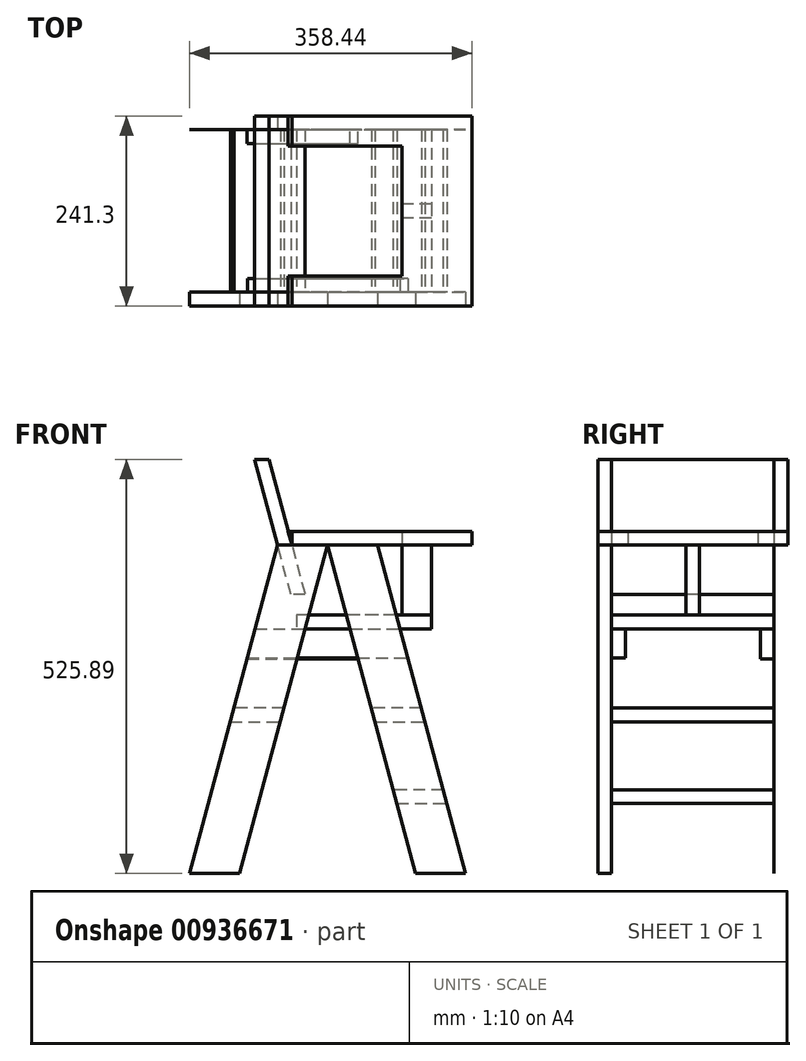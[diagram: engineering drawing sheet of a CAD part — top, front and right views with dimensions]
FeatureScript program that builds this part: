
annotation { "Feature Type Name" : "Feature", "Feature Type Description" : "" }
export const myFeature = defineFeature(function(context is Context, id is Id, definition is map)
    precondition{}
    {
        {
            var Q0;
            Q0=qCreatedBy(makeId("Front.planeOp"),FACE);
            var sketch = newSketch(context, id + "F0", { "sketchPlane" : qUnion([Q0])});
            skLineSegment(sketch, "E0", {"start": v(0, 0) * mm, "end": v(63.5, 0) * mm});
            skLineSegment(sketch, "E1", {"start": v(63.5, 0) * mm, "end": v(175.26, 417.09) * mm});
            skLineSegment(sketch, "E2", {"start": v(175.26, 417.09) * mm, "end": v(111.76, 417.09) * mm});
            skLineSegment(sketch, "E3", {"start": v(111.76, 417.09) * mm, "end": v(0, 0) * mm});
            skLineSegment(sketch, "E4", {"start": v(287.02, 0) * mm, "end": v(350.52, 0) * mm});
            skLineSegment(sketch, "E5", {"start": v(350.52, 0) * mm, "end": v(238.76, 417.09) * mm});
            skLineSegment(sketch, "E6", {"start": v(238.76, 417.09) * mm, "end": v(175.26, 417.09) * mm});
            skLineSegment(sketch, "E7", {"start": v(175.26, 417.09) * mm, "end": v(287.02, 0) * mm});
            skSolve(sketch);
        }
        {
            var Q0;
            Q0 = qSketchRegion(id + "F0", true);
            extrude(context, id + "F1", {"entities" : qUnion([Q0]), "oppositeDirection" : true, "depth" : 17.46 * mm, "offsetDistance" : 25.4 * mm});
        }
        {
            var Q0;
            Q0=makeQuery(id+"F1.opExtrude","CAP_FACE",FACE,{"disambiguationData":[OSD([sQuery(id+"F0.wireOp",EDGE,"E0"),sQuery(id+"F0.wireOp",EDGE,"E1"),sQuery(id+"F0.wireOp",EDGE,"E2"),sQuery(id+"F0.wireOp",EDGE,"E3")])],"isStart":false});
            cPlane(context, id + "F2", {"entities" : qUnion([Q0]), "cplaneType" : CPlaneType.OFFSET, "offset" : 0 * mm, "width" : 152.4 * mm, "height" : 152.4 * mm});
        }
        {
            var Q0;
            Q0=makeQuery(id+"F1.opExtrude","SWEPT_FACE",FACE,{"disambiguationData":[OSD([sQuery(id+"F0.wireOp",EDGE,"E2")])]});
            cPlane(context, id + "F3", {"entities" : qUnion([Q0]), "cplaneType" : CPlaneType.OFFSET, "offset" : 0 * mm, "width" : 152.4 * mm, "height" : 152.4 * mm});
        }
        {
            var Q0;
            Q0=qCreatedBy(id+"F2.planeOp",FACE);
            var sketch = newSketch(context, id + "F4", { "sketchPlane" : qUnion([Q0])});
            skLineSegment(sketch, "E8", {"start": v(-146.7, 354.15) * mm, "end": v(-128.62, 354.15) * mm});
            skLineSegment(sketch, "E9", {"start": v(-128.62, 354.15) * mm, "end": v(-82.6, 525.9) * mm});
            skLineSegment(sketch, "E10", {"start": v(-82.6, 525.9) * mm, "end": v(-100.68, 525.9) * mm});
            skLineSegment(sketch, "E11", {"start": v(-100.68, 525.9) * mm, "end": v(-146.7, 354.15) * mm});
            skPoint(sketch, "E12.0", {"position": v(-111.76, 417.09) * mm});
            skLineSegment(sketch, "E13.0", {"start": v(-129.84, 417.09) * mm, "end": v(-111.76, 417.09) * mm});
            skSolve(sketch);
        }
        {
            var Q0;
            Q0 = qSketchRegion(id + "F4", true);
            extrude(context, id + "F5", {"entities" : qUnion([Q0]), "depth" : 206.38 * mm, "offsetDistance" : 25.4 * mm});
        }
        {
            var Q0;
            Q0=qCreatedBy(id+"F3.planeOp",FACE);
            var sketch = newSketch(context, id + "F6", { "sketchPlane" : qUnion([Q0])});
            skLineSegment(sketch, "E14", {"start": v(129.84, 0) * mm, "end": v(358.44, 0) * mm});
            skLineSegment(sketch, "E15", {"start": v(358.44, 0) * mm, "end": v(358.44, 241.3) * mm});
            skLineSegment(sketch, "E16", {"start": v(358.44, 241.3) * mm, "end": v(129.84, 241.3) * mm});
            skLineSegment(sketch, "E17", {"start": v(129.84, 241.3) * mm, "end": v(129.84, 203.2) * mm});
            skLineSegment(sketch, "E18", {"start": v(129.84, 203.2) * mm, "end": v(269.54, 203.2) * mm});
            skLineSegment(sketch, "E19", {"start": v(269.54, 203.2) * mm, "end": v(269.54, 38.1) * mm});
            skLineSegment(sketch, "E20", {"start": v(269.54, 38.1) * mm, "end": v(129.84, 38.1) * mm});
            skLineSegment(sketch, "E21", {"start": v(129.84, 38.1) * mm, "end": v(129.84, 0) * mm});
            skLineSegment(sketch, "E22.0", {"start": v(175.26, 17.46) * mm, "end": v(111.76, 17.46) * mm});
            skLineSegment(sketch, "E23", {"start": v(143.5, 17.46) * mm, "end": v(129.84, 17.46) * mm});
            skSolve(sketch);
        }
        {
            var Q0;
            Q0 = qSketchRegion(id + "F6", true);
            extrude(context, id + "F7", {"entities" : qUnion([Q0]), "depth" : 17.46 * mm, "offsetDistance" : 25.4 * mm});
        }
        {
            var Q0;
            Q0=makeQuery(id+"F7.opExtrude","SWEPT_FACE",FACE,{"disambiguationData":[OSD([sQuery(id+"F6.wireOp",EDGE,"E21")])]});
            var Q1;
            Q1=makeQuery(id+"F7.opExtrude","SWEPT_FACE",FACE,{"disambiguationData":[OSD([sQuery(id+"F6.wireOp",EDGE,"E17")])]});
            var Q2;
            Q2=makeQuery(id+"F5.opExtrude","SWEPT_FACE",FACE,{"disambiguationData":[OSD([sQuery(id+"F4.wireOp",EDGE,"E11")])]});
            extrude(context, id + "F8", {"entities" : qUnion([Q0, Q1]), "endBound" : BoundingType.UP_TO_SURFACE, "depth" : 25.4 * mm, "endBoundEntityFace" : qUnion([Q2]), "offsetDistance" : 25.4 * mm});
        }
        {
            var Q0;
            Q0=makeQuery(id+"F1.opExtrude","CAP_FACE",FACE,{"disambiguationData":[OSD([sQuery(id+"F0.wireOp",EDGE,"E4"),sQuery(id+"F0.wireOp",EDGE,"E5"),sQuery(id+"F0.wireOp",EDGE,"E6"),sQuery(id+"F0.wireOp",EDGE,"E7")])],"isStart":false});
            var sketch = newSketch(context, id + "F9", { "sketchPlane" : qUnion([Q0])});
            skLineSegment(sketch, "E24.0.1", {"start": v(-135.58, 310.72) * mm, "end": v(-307.03, 310.72) * mm});
            skLineSegment(sketch, "E24.0.2", {"start": v(-307.03, 310.72) * mm, "end": v(-307.03, 328.19) * mm});
            skLineSegment(sketch, "E24.0.3", {"start": v(-307.03, 328.19) * mm, "end": v(-135.58, 328.19) * mm});
            skLineSegment(sketch, "E25.0", {"start": v(-135.58, 328.19) * mm, "end": v(-135.58, 310.72) * mm});
            skLineSegment(sketch, "E26.0", {"start": v(-63.5, 0) * mm, "end": v(-175.26, 417.09) * mm});
            skPoint(sketch, "E27", {"position": v(-146.76, 310.72) * mm});
            skLineSegment(sketch, "E28.0", {"start": v(-100.68, 525.9) * mm, "end": v(-146.7, 354.15) * mm});
            skLineSegment(sketch, "E29", {"start": v(-146.7, 354.15) * mm, "end": v(-153.66, 328.19) * mm});
            skLineSegment(sketch, "E30.0", {"start": v(-128.62, 354.15) * mm, "end": v(-82.6, 525.9) * mm});
            skLineSegment(sketch, "E31", {"start": v(-128.62, 354.15) * mm, "end": v(-135.58, 328.19) * mm});
            skSolve(sketch);
        }
        {
            var Q0;
            {var subQ0=sQuery(id+"F9.wireOp",EDGE,"E25.0");Q0=makeQuery(id+"F9.imprint","IMPRINT",FACE,{"disambiguationData":[TD([[makeQuery(id+"F9.imprint","IMPRINT",EDGE,{"derivedFrom":subQ0}),-1.0]])]});}
            var Q1;
            {var subQ0=sQuery(id+"F9.wireOp",EDGE,"E26.0");var subQ1=sQuery(id+"F9.wireOp",EDGE,"E24.0.1");var subQ2=makeQuery(id+"F9.imprint","INTERSECT",VERTEX,{"derivedFrom":[subQ1,subQ0]});Q1=makeQuery(id+"F9.imprint","IMPRINT",FACE,{"disambiguationData":[TD([[makeQuery(id+"F9.imprint","IMPRINT",EDGE,{"disambiguationData":[TD([[subQ2,-1.0]])],"derivedFrom":subQ1}),-1.0]])]});}
            var Q2;
            {var subQ0=sQuery(id+"F9.wireOp",EDGE,"E24.0.1");var subQ1=makeQuery(id+"F1.opExtrude","CAP_EDGE",EDGE,{"disambiguationData":[OSD([sQuery(id+"F0.wireOp",EDGE,"E7")])],"isStart":false});var subQ2=makeQuery(id+"F9.imprint","INTERSECT",VERTEX,{"derivedFrom":[subQ1,subQ0]});Q2=makeQuery(id+"F9.imprint","IMPRINT",FACE,{"disambiguationData":[TD([[makeQuery(id+"F9.imprint","IMPRINT",EDGE,{"disambiguationData":[TD([[subQ2,-1.0]])],"derivedFrom":subQ0}),-1.0]])]});}
            var Q3;
            {var subQ0=sQuery(id+"F9.wireOp",EDGE,"E24.0.2");Q3=makeQuery(id+"F9.imprint","IMPRINT",FACE,{"disambiguationData":[TD([[makeQuery(id+"F9.imprint","IMPRINT",EDGE,{"derivedFrom":subQ0}),-1.0]])]});}
            extrude(context, id + "F10", {"entities" : qUnion([Q0, Q1, Q2, Q3]), "depth" : 206.38 * mm, "offsetDistance" : 25.4 * mm});
        }
        {
            var Q0;
            Q0=makeQuery(id+"F1.opExtrude","CAP_FACE",FACE,{"disambiguationData":[OSD([sQuery(id+"F0.wireOp",EDGE,"E0"),sQuery(id+"F0.wireOp",EDGE,"E1"),sQuery(id+"F0.wireOp",EDGE,"E2"),sQuery(id+"F0.wireOp",EDGE,"E3")])],"isStart":false});
            var sketch = newSketch(context, id + "F11", { "sketchPlane" : qUnion([Q0])});
            skLineSegment(sketch, "E32.0", {"start": v(-83.26, 310.72) * mm, "end": v(-73.32, 273.64) * mm});
            skLineSegment(sketch, "E33.0", {"start": v(-277.2, 273.64) * mm, "end": v(-267.26, 310.72) * mm});
            skLineSegment(sketch, "E34.0", {"start": v(-135.58, 310.72) * mm, "end": v(-267.26, 310.72) * mm});
            skLineSegment(sketch, "E35", {"start": v(-135.58, 310.72) * mm, "end": v(-83.26, 310.72) * mm});
            skLineSegment(sketch, "E36", {"start": v(-73.32, 273.64) * mm, "end": v(-277.2, 273.64) * mm});
            skSolve(sketch);
        }
        {
            var Q0;
            Q0 = qSketchRegion(id + "F11", true);
            extrude(context, id + "F12", {"entities" : qUnion([Q0]), "depth" : 17.46 * mm, "offsetDistance" : 25.4 * mm});
        }
        {
            var Q0;
            Q0=makeQuery(id+"F10.opExtrude","CAP_FACE",FACE,{"disambiguationData":[OSD([sQuery(id+"F9.wireOp",EDGE,"E24.0.1"),sQuery(id+"F9.wireOp",EDGE,"E24.0.2"),sQuery(id+"F9.wireOp",EDGE,"E24.0.3"),sQuery(id+"F9.wireOp",EDGE,"E25.0")])],"isStart":false});
            var sketch = newSketch(context, id + "F13", { "sketchPlane" : qUnion([Q0])});
            skLineSegment(sketch, "E37.0.0", {"start": v(-175.26, 417.09) * mm, "end": v(-238.76, 417.09) * mm});
            skLineSegment(sketch, "E37.0.1", {"start": v(-238.76, 417.09) * mm, "end": v(-350.52, 0) * mm});
            skLineSegment(sketch, "E37.0.2", {"start": v(-350.52, 0) * mm, "end": v(-287.02, 0) * mm});
            skLineSegment(sketch, "E37.0.3", {"start": v(-287.02, 0) * mm, "end": v(-175.26, 417.09) * mm});
            skLineSegment(sketch, "E38.0.0", {"start": v(-111.76, 417.09) * mm, "end": v(-175.26, 417.09) * mm});
            skLineSegment(sketch, "E38.0.1", {"start": v(-175.26, 417.09) * mm, "end": v(-63.5, 0) * mm});
            skLineSegment(sketch, "E38.0.2", {"start": v(-63.5, 0) * mm, "end": v(0, 0) * mm});
            skLineSegment(sketch, "E38.0.3", {"start": v(0, 0) * mm, "end": v(-111.76, 417.09) * mm});
            skSolve(sketch);
        }
        {
            var Q0;
            Q0 = qSketchRegion(id + "F13", true);
            extrude(context, id + "F14", {"entities" : qUnion([Q0]), "depth" : 11 / 406.4 * mm, "offsetDistance" : 25.4 * mm});
        }
        {
            var Q0;
            {var subQ0=sQuery(id+"F4.wireOp",EDGE,"E10");Q0=makeQuery(id+"F4.imprint","IMPRINT",FACE,{"disambiguationData":[TD([[makeQuery(id+"F4.imprint","IMPRINT",EDGE,{"derivedFrom":subQ0}),1.0]])]});}
            extrude(context, id + "F15", {"entities" : qUnion([Q0]), "oppositeDirection" : true, "depth" : 17.46 * mm, "offsetDistance" : 25.4 * mm});
        }
        {
            var Q0;
            Q0=makeQuery(id+"F5.opExtrude","CAP_FACE",FACE,{"disambiguationData":[OSD([sQuery(id+"F4.wireOp",EDGE,"E8"),sQuery(id+"F4.wireOp",EDGE,"E9"),sQuery(id+"F4.wireOp",EDGE,"E10"),sQuery(id+"F4.wireOp",EDGE,"E11")])],"isStart":false});
            var sketch = newSketch(context, id + "F16", { "sketchPlane" : qUnion([Q0])});
            skLineSegment(sketch, "E39.0.0", {"start": v(-128.62, 354.15) * mm, "end": v(-82.6, 525.9) * mm});
            skLineSegment(sketch, "E39.0.1", {"start": v(-82.6, 525.9) * mm, "end": v(-100.68, 525.9) * mm});
            skLineSegment(sketch, "E39.0.2", {"start": v(-100.68, 525.9) * mm, "end": v(-146.7, 354.15) * mm});
            skLineSegment(sketch, "E39.0.3", {"start": v(-146.7, 354.15) * mm, "end": v(-128.62, 354.15) * mm});
            skLineSegment(sketch, "E40.0", {"start": v(-111.76, 417.09) * mm, "end": v(-175.26, 417.09) * mm});
            skSolve(sketch);
        }
        {
            var Q0;
            {var subQ0=sQuery(id+"F16.wireOp",EDGE,"E39.0.1");Q0=makeQuery(id+"F16.imprint","IMPRINT",FACE,{"disambiguationData":[TD([[makeQuery(id+"F16.imprint","IMPRINT",EDGE,{"derivedFrom":subQ0}),1.0]])]});}
            extrude(context, id + "F17", {"entities" : qUnion([Q0]), "depth" : 17.46 * mm, "offsetDistance" : 25.4 * mm});
        }
        {
            var Q0;
            Q0=makeQuery(id+"F14.opExtrude","CAP_FACE",FACE,{"disambiguationData":[OSD([sQuery(id+"F13.wireOp",EDGE,"E38.0.0"),sQuery(id+"F13.wireOp",EDGE,"E38.0.1"),sQuery(id+"F13.wireOp",EDGE,"E38.0.2"),sQuery(id+"F13.wireOp",EDGE,"E38.0.3")])],"isStart":true});
            var sketch = newSketch(context, id + "F18", { "sketchPlane" : qUnion([Q0])});
            skLineSegment(sketch, "E41.0.0", {"start": v(175.26, 417.09) * mm, "end": v(111.76, 417.09) * mm});
            skLineSegment(sketch, "E41.0.1", {"start": v(111.76, 417.09) * mm, "end": v(0, 0) * mm});
            skLineSegment(sketch, "E41.0.2", {"start": v(0, 0) * mm, "end": v(63.5, 0) * mm});
            skLineSegment(sketch, "E41.0.3", {"start": v(63.5, 0) * mm, "end": v(175.26, 417.09) * mm});
            skLineSegment(sketch, "E42.0.0", {"start": v(287.02, 0) * mm, "end": v(350.52, 0) * mm});
            skLineSegment(sketch, "E42.0.1", {"start": v(350.52, 0) * mm, "end": v(238.76, 417.09) * mm});
            skLineSegment(sketch, "E42.0.2", {"start": v(238.76, 417.09) * mm, "end": v(175.26, 417.09) * mm});
            skLineSegment(sketch, "E42.0.3", {"start": v(175.26, 417.09) * mm, "end": v(287.02, 0) * mm});
            skLineSegment(sketch, "E43.0", {"start": v(135.58, 310.72) * mm, "end": v(307.03, 310.72) * mm});
            skLineSegment(sketch, "E44", {"start": v(135.58, 310.72) * mm, "end": v(83.26, 310.72) * mm});
            skLineSegment(sketch, "E45", {"start": v(83.26, 310.72) * mm, "end": v(73.05, 272.62) * mm});
            skLineSegment(sketch, "E46", {"start": v(73.05, 272.62) * mm, "end": v(277.47, 272.62) * mm});
            skLineSegment(sketch, "E47", {"start": v(277.47, 272.62) * mm, "end": v(267.26, 310.72) * mm});
            skSolve(sketch);
        }
        {
            var Q0;
            {var subQ1=sQuery(id+"F18.wireOp",EDGE,"E44");Q0=makeQuery(id+"F18.imprint","IMPRINT",FACE,{"disambiguationData":[TD([[makeQuery(id+"F18.imprint","IMPRINT",EDGE,{"derivedFrom":subQ1}),1.0]])]});}
            var Q1;
            {var subQ0=sQuery(id+"F18.wireOp",EDGE,"E46");var subQ1=sQuery(id+"F18.wireOp",EDGE,"E41.0.3");var subQ2=makeQuery(id+"F18.imprint","INTERSECT",VERTEX,{"derivedFrom":[subQ1,subQ0]});Q1=makeQuery(id+"F18.imprint","IMPRINT",FACE,{"disambiguationData":[TD([[makeQuery(id+"F18.imprint","IMPRINT",EDGE,{"disambiguationData":[TD([[subQ2,1.0]])],"derivedFrom":subQ1}),1.0]])]});}
            var Q2;
            {var subQ5=sQuery(id+"F18.wireOp",EDGE,"E47");Q2=makeQuery(id+"F18.imprint","IMPRINT",FACE,{"disambiguationData":[TD([[makeQuery(id+"F18.imprint","IMPRINT",EDGE,{"derivedFrom":subQ5}),1.0]])]});}
            extrude(context, id + "F19", {"entities" : qUnion([Q0, Q1, Q2]), "depth" : 17.46 * mm, "offsetDistance" : 25.4 * mm});
        }
        {
            var Q0;
            Q0=makeQuery(id+"F1.opExtrude","CAP_FACE",FACE,{"disambiguationData":[OSD([sQuery(id+"F0.wireOp",EDGE,"E4"),sQuery(id+"F0.wireOp",EDGE,"E5"),sQuery(id+"F0.wireOp",EDGE,"E6"),sQuery(id+"F0.wireOp",EDGE,"E7")])],"isStart":false});
            var sketch = newSketch(context, id + "F20", { "sketchPlane" : qUnion([Q0])});
            skLineSegment(sketch, "E48.0.0", {"start": v(-175.26, 417.09) * mm, "end": v(-238.76, 417.09) * mm});
            skLineSegment(sketch, "E48.0.1", {"start": v(-238.76, 417.09) * mm, "end": v(-350.52, 0) * mm});
            skLineSegment(sketch, "E48.0.2", {"start": v(-350.52, 0) * mm, "end": v(-287.02, 0) * mm});
            skLineSegment(sketch, "E48.0.3", {"start": v(-287.02, 0) * mm, "end": v(-175.26, 417.09) * mm});
            skLineSegment(sketch, "E49", {"start": v(-294.2, 210.14) * mm, "end": v(-230.7, 210.14) * mm});
            skLineSegment(sketch, "E50", {"start": v(-230.7, 210.14) * mm, "end": v(-235.39, 192.68) * mm});
            skLineSegment(sketch, "E51", {"start": v(-235.39, 192.68) * mm, "end": v(-298.89, 192.68) * mm});
            skLineSegment(sketch, "E52", {"start": v(-298.89, 192.68) * mm, "end": v(-294.2, 210.14) * mm});
            skLineSegment(sketch, "E53", {"start": v(-322.02, 106.36) * mm, "end": v(-258.52, 106.36) * mm});
            skLineSegment(sketch, "E54", {"start": v(-258.52, 106.36) * mm, "end": v(-263.2, 88.9) * mm});
            skLineSegment(sketch, "E55", {"start": v(-263.2, 88.9) * mm, "end": v(-326.7, 88.9) * mm});
            skLineSegment(sketch, "E56", {"start": v(-326.7, 88.9) * mm, "end": v(-322.02, 106.36) * mm});
            skLineSegment(sketch, "E57.0.0", {"start": v(-111.76, 417.09) * mm, "end": v(-175.26, 417.09) * mm});
            skLineSegment(sketch, "E57.0.1", {"start": v(-175.26, 417.09) * mm, "end": v(-63.5, 0) * mm});
            skLineSegment(sketch, "E57.0.2", {"start": v(-63.5, 0) * mm, "end": v(0, 0) * mm});
            skLineSegment(sketch, "E57.0.3", {"start": v(0, 0) * mm, "end": v(-111.76, 417.09) * mm});
            skLineSegment(sketch, "E58", {"start": v(-119.8, 210.14) * mm, "end": v(-56.3, 210.14) * mm});
            skLineSegment(sketch, "E59", {"start": v(-56.3, 210.14) * mm, "end": v(-51.63, 192.68) * mm});
            skLineSegment(sketch, "E60", {"start": v(-51.63, 192.68) * mm, "end": v(-115.13, 192.68) * mm});
            skLineSegment(sketch, "E61", {"start": v(-115.13, 192.68) * mm, "end": v(-119.8, 210.14) * mm});
            skSolve(sketch);
        }
        {
            var Q0;
            Q0=makeQuery(id+"F20.imprint","IMPRINT",FACE,{"disambiguationData":[TD([[makeQuery(id+"F20.imprint","IMPRINT",EDGE,{"derivedFrom":sQuery(id+"F20.wireOp",EDGE,"E49")}),-1.0]])]});
            var Q1;
            Q1=makeQuery(id+"F20.imprint","IMPRINT",FACE,{"disambiguationData":[TD([[makeQuery(id+"F20.imprint","IMPRINT",EDGE,{"derivedFrom":sQuery(id+"F20.wireOp",EDGE,"E53")}),-1.0]])]});
            var Q2;
            Q2=makeQuery(id+"F20.imprint","IMPRINT",FACE,{"disambiguationData":[TD([[makeQuery(id+"F20.imprint","IMPRINT",EDGE,{"derivedFrom":sQuery(id+"F20.wireOp",EDGE,"E58")}),-1.0]])]});
            extrude(context, id + "F21", {"entities" : qUnion([Q0, Q1, Q2]), "depth" : 206.38 * mm, "offsetDistance" : 25.4 * mm});
        }
        {
            var Q0;
            Q0=makeQuery(id+"F10.opExtrude","SWEPT_FACE",FACE,{"disambiguationData":[OSD([sQuery(id+"F9.wireOp",EDGE,"E24.0.3")])]});
            var sketch = newSketch(context, id + "F22", { "sketchPlane" : qUnion([Q0])});
            skLineSegment(sketch, "E62.0.0", {"start": v(135.58, 17.46) * mm, "end": v(307.03, 17.46) * mm});
            skLineSegment(sketch, "E62.0.1", {"start": v(307.03, 17.46) * mm, "end": v(307.03, 223.84) * mm});
            skLineSegment(sketch, "E62.0.2", {"start": v(307.03, 223.84) * mm, "end": v(135.58, 223.84) * mm});
            skLineSegment(sketch, "E62.0.3", {"start": v(135.58, 223.84) * mm, "end": v(135.58, 17.46) * mm});
            skLineSegment(sketch, "E63.bottom", {"start": v(307.03, 111.92) * mm, "end": v(269.94, 111.92) * mm});
            skLineSegment(sketch, "E63.top", {"start": v(307.03, 129.38) * mm, "end": v(269.94, 129.38) * mm});
            skLineSegment(sketch, "E63.left", {"start": v(307.03, 111.92) * mm, "end": v(307.03, 129.38) * mm});
            skLineSegment(sketch, "E63.right", {"start": v(269.94, 111.92) * mm, "end": v(269.94, 129.38) * mm});
            skLineSegment(sketch, "E64", {"start": v(307.03, 120.65) * mm, "end": v(269.94, 120.65) * mm});
            skSolve(sketch);
        }
        {
            var Q0;
            {var subQ0=sQuery(id+"F22.wireOp",EDGE,"E63.top");Q0=makeQuery(id+"F22.imprint","IMPRINT",FACE,{"disambiguationData":[TD([[makeQuery(id+"F22.imprint","IMPRINT",EDGE,{"derivedFrom":subQ0}),1.0]])]});}
            var Q1;
            {var subQ0=sQuery(id+"F22.wireOp",EDGE,"E63.bottom");Q1=makeQuery(id+"F22.imprint","IMPRINT",FACE,{"disambiguationData":[TD([[makeQuery(id+"F22.imprint","IMPRINT",EDGE,{"derivedFrom":subQ0}),-1.0]])]});}
            extrude(context, id + "F23", {"entities" : qUnion([Q0, Q1]), "depth" : 88.9 * mm, "offsetDistance" : 25.4 * mm});
        }
    });
